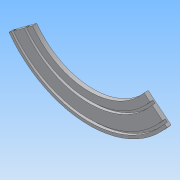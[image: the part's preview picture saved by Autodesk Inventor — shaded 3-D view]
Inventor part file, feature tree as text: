
AUTODESK INVENTOR PART (.ipt)
format: ipt  version: 2013 (Build 170138000, 138)  size: 151,040 bytes
history: native  units: in
note: dims shown in document units (in); Inventor stores cm internally (conversion verified against a paired STEP export)
features: extrude x2, plane x1, other x1, reference x1, sketch x1
ambient origin geometry x8: Origin, YZ Plane, XZ Plane, XY Plane, X Axis, Y Axis, Z Axis, Center Point
bodies: Solid1 (feature_tree)
feature tree (6):
  plane  "Work Plane1"
  other  "ThermoBulbBorder"
  extrude  "Extrusion2"  Depth=2.5in
  extrude  "Extrusion3"  Depth=2.5in
  reference  "Reference2"
  sketch  "Sketch2"  dims[d0=24.0in d5=2.5in d6=2.5in d7=33.0in d8=0.48in d9=0.48in d10=2.25in d11=1.29in d12=6.0in d13=0.71in d14=0.0in d15=0.48in d17=0.5in d18=2.25in d19=0.48in d20=0.5in d21=0.0in]
